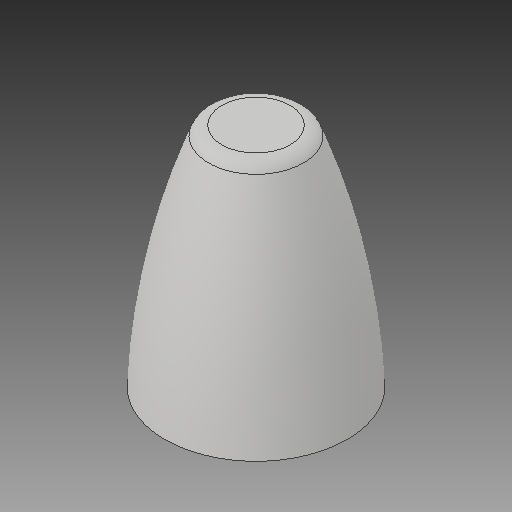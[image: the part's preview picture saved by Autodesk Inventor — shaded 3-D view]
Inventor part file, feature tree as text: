
AUTODESK INVENTOR PART (.ipt)
format: ipt  version: 2018 (Build 220112000, 112)  size: 165,888 bytes
history: native  units: in
note: dims shown in document units (in); Inventor stores cm internally (conversion verified against a paired STEP export)
features: fillet x1
ambient origin geometry x8: Origin, YZ Plane, XZ Plane, XY Plane, X Axis, Y Axis, Z Axis, Center Point
bodies: Solid1 (feature_tree)
feature tree (1):
  fillet  "Fillet3"  [1 undecoded]
note: 1 required parameter value undecoded (feature->parameter linkage not recoverable at this tier; creation-order binding heuristic only, values carry confidence <= 0.55)
